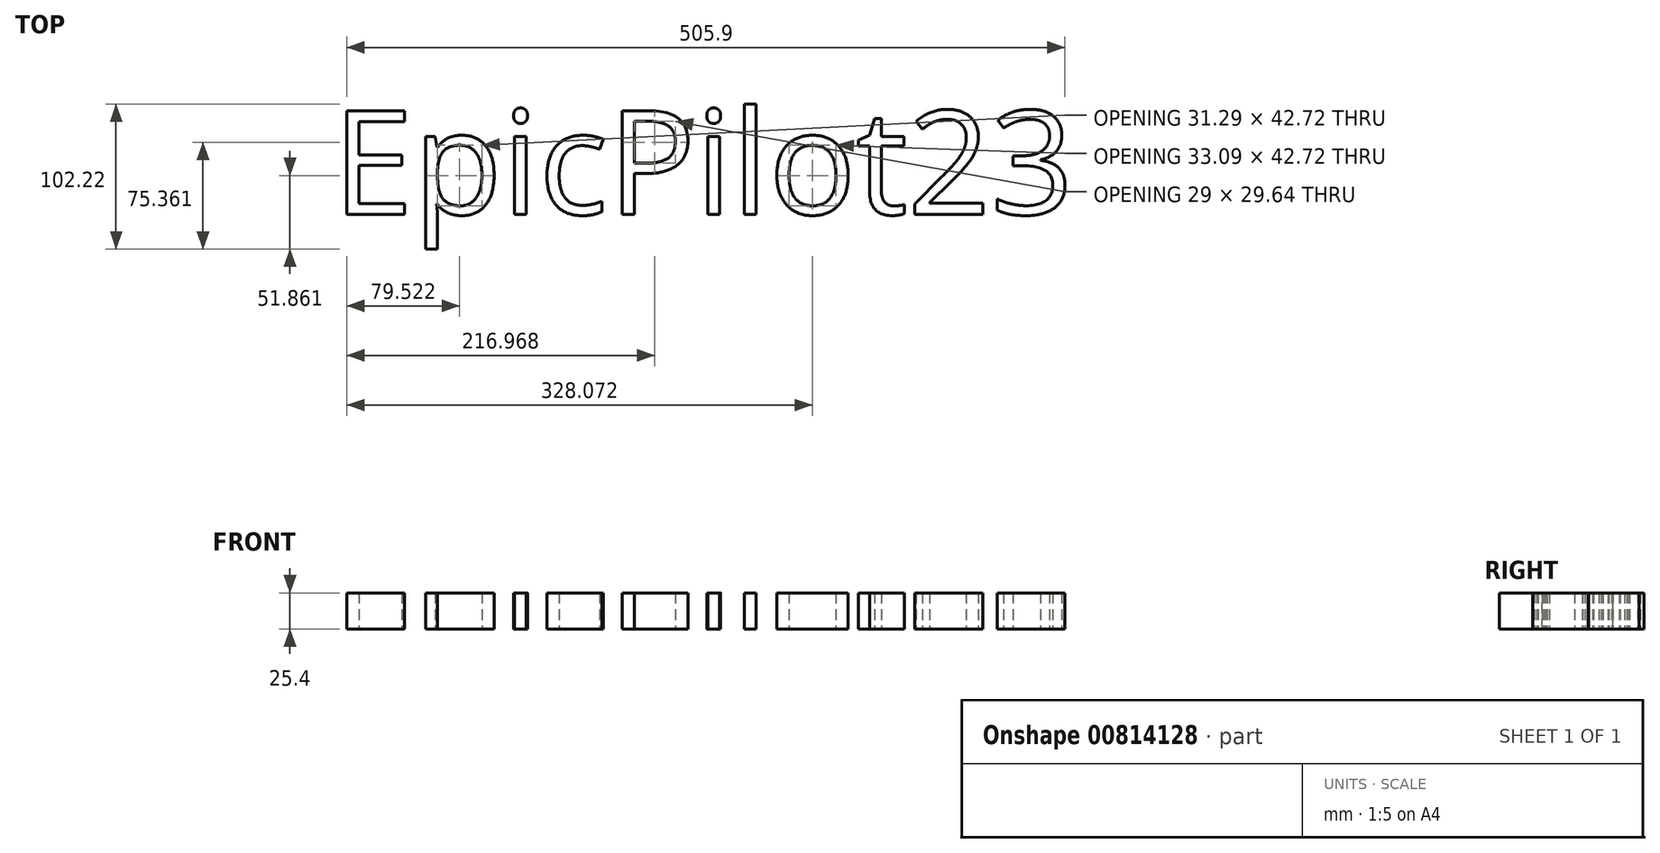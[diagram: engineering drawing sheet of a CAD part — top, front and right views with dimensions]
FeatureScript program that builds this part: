
annotation { "Feature Type Name" : "Feature", "Feature Type Description" : "" }
export const myFeature = defineFeature(function(context is Context, id is Id, definition is map)
    precondition{}
    {
        {
            var Q0;
            Q0=qCreatedBy(makeId("Top.planeOp"),FACE);
            var sketch = newSketch(context, id + "F0", { "sketchPlane" : qUnion([Q0])});
            skText(sketch, "E0", { "text": "EpicPilot23\n", "fontName": "OpenSans-Regular.ttf"});
            const initialGuessF0  = {"E0": [-0.06356, -0.02755, 1, 0, 0.07359]};
            skSetInitialGuess(sketch, initialGuessF0);
            skSolve(sketch);
        }
        {
            var Q0;
            Q0 = qSketchRegion(id + "F0", true);
            extrude(context, id + "F1", {"entities" : qUnion([Q0]), "depth" : 25.4 * mm, "offsetDistance" : 25.4 * mm});
        }
    });
